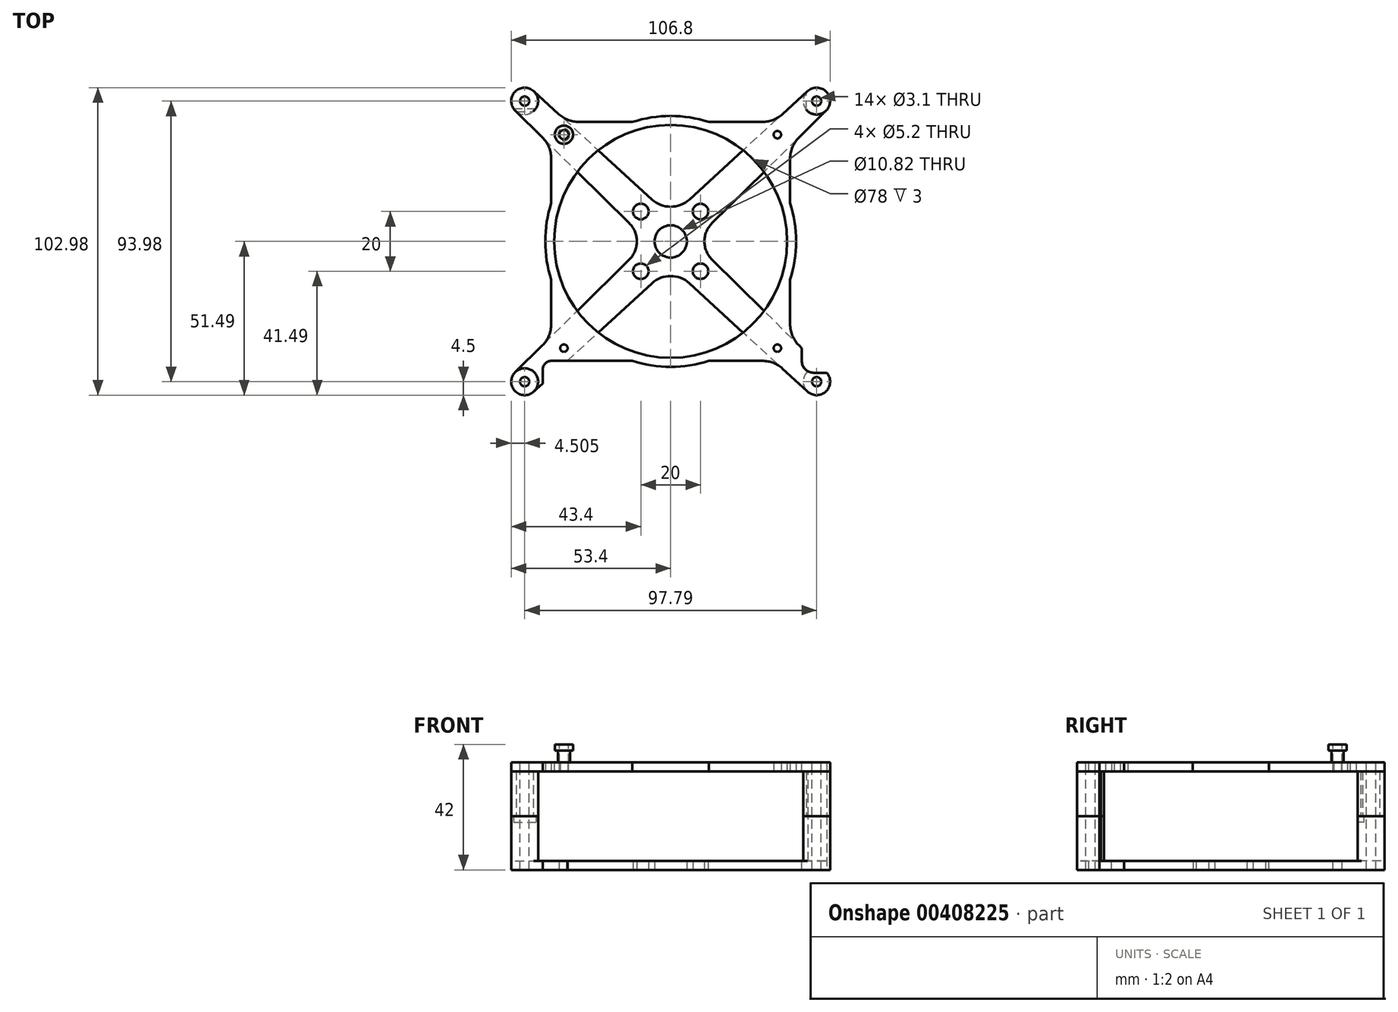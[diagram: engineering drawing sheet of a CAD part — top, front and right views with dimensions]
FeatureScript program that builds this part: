
annotation { "Feature Type Name" : "Feature", "Feature Type Description" : "" }
export const myFeature = defineFeature(function(context is Context, id is Id, definition is map)
    precondition{}
    {
        {
            var Q0;
            Q0=qCreatedBy(makeId("Top.planeOp"),FACE);
            var sketch = newSketch(context, id + "F0", { "sketchPlane" : qUnion([Q0])});
            skLineSegment(sketch, "E0.rect.bottom", {"start": v(48.9, 46.99) * mm, "end": v(-48.9, 46.99) * mm, "construction": true});
            skLineSegment(sketch, "E0.rect.top", {"start": v(48.9, -47) * mm, "end": v(-48.9, -47) * mm, "construction": true});
            skLineSegment(sketch, "E0.rect.left", {"start": v(48.9, 46.99) * mm, "end": v(48.9, -47) * mm, "construction": true});
            skLineSegment(sketch, "E0.rect.right", {"start": v(-48.9, 46.99) * mm, "end": v(-48.9, -47) * mm, "construction": true});
            skPoint(sketch, "E0.rect.middle", {"position": v(0, 0) * mm});
            skLineSegment(sketch, "E1.rect.bottom", {"start": v(10, 10) * mm, "end": v(-10, 10) * mm, "construction": true});
            skLineSegment(sketch, "E1.rect.top", {"start": v(10, -10) * mm, "end": v(-10, -10) * mm, "construction": true});
            skLineSegment(sketch, "E1.rect.left", {"start": v(10, 10) * mm, "end": v(10, -10) * mm, "construction": true});
            skLineSegment(sketch, "E1.rect.right", {"start": v(-10, 10) * mm, "end": v(-10, -10) * mm, "construction": true});
            skCircle(sketch, "E2", {"center": v(-10, 10) * mm, "radius": 2.6 * mm});
            skCircle(sketch, "E3", {"center": v(10, 10) * mm, "radius": 2.6 * mm});
            skCircle(sketch, "E4", {"center": v(10, -10) * mm, "radius": 2.6 * mm});
            skCircle(sketch, "E5", {"center": v(-10, -10) * mm, "radius": 2.6 * mm});
            skArc(sketch, "E6", {"start": v(-45.86, 50.3) * mm, "mid": v(-52.16, 50.1) * mm, "end": v(-52.06, 43.79) * mm});
            skArc(sketch, "E7", {"start": v(52.06, 43.79) * mm, "mid": v(52.16, 50.1) * mm, "end": v(45.86, 50.3) * mm});
            skArc(sketch, "E8", {"start": v(45.86, -50.3) * mm, "mid": v(52.16, -50.1) * mm, "end": v(52.06, -43.79) * mm});
            skArc(sketch, "E9", {"start": v(-52.06, -43.79) * mm, "mid": v(-52.16, -50.1) * mm, "end": v(-45.86, -50.3) * mm});
            skCircle(sketch, "E10", {"center": v(-10, -10) * mm, "radius": 5.5 * mm, "construction": true});
            skCircle(sketch, "E11", {"center": v(10, -10) * mm, "radius": 5.5 * mm, "construction": true});
            skCircle(sketch, "E12", {"center": v(-10, 10) * mm, "radius": 5.5 * mm, "construction": true});
            skCircle(sketch, "E13", {"center": v(10, 10) * mm, "radius": 5.5 * mm, "construction": true});
            skArc(sketch, "E14", {"start": v(-13.86, -6.09) * mm, "mid": v(-11.32, 0) * mm, "end": v(-13.86, 6.09) * mm});
            skLineSegment(sketch, "E15", {"start": v(-52.06, -43.79) * mm, "end": v(-13.86, -6.09) * mm});
            skLineSegment(sketch, "E16", {"start": v(-45.86, -50.3) * mm, "end": v(-6.28, -14.06) * mm});
            skLineSegment(sketch, "E17", {"start": v(45.86, 50.3) * mm, "end": v(6.28, 14.06) * mm});
            skLineSegment(sketch, "E18", {"start": v(52.06, 43.79) * mm, "end": v(13.86, 6.09) * mm});
            skLineSegment(sketch, "E19", {"start": v(-52.06, 43.79) * mm, "end": v(-13.86, 6.09) * mm});
            skLineSegment(sketch, "E20", {"start": v(-45.86, 50.3) * mm, "end": v(-6.28, 14.06) * mm});
            skLineSegment(sketch, "E21", {"start": v(45.86, -50.3) * mm, "end": v(6.28, -14.06) * mm});
            skLineSegment(sketch, "E22", {"start": v(52.06, -43.79) * mm, "end": v(13.86, -6.09) * mm});
            skArc(sketch, "E23", {"start": v(-6.28, 14.06) * mm, "mid": v(0, 11.61) * mm, "end": v(6.28, 14.06) * mm});
            skArc(sketch, "E24", {"start": v(13.86, 6.09) * mm, "mid": v(11.32, 0) * mm, "end": v(13.86, -6.09) * mm});
            skArc(sketch, "E25", {"start": v(6.28, -14.06) * mm, "mid": v(0, -11.61) * mm, "end": v(-6.28, -14.06) * mm});
            skCircle(sketch, "E26", {"center": v(0, 0) * mm, "radius": 5.4 * mm});
            skSolve(sketch);
        }
        {
            var Q0;
            Q0=qSketchRegion(id+"F0",true);
            extrude(context, id + "F1", {"entities" : qUnion([Q0]), "depth" : 3 * mm});
        }
        {
            var Q0;
            Q0=makeQuery(id+"F1.opExtrude","CAP_FACE",FACE,{"disambiguationData":[OSD([sQuery(id+"F0.wireOp",EDGE,"d0fabe0d-cebb-4a5e-acc7-4882b4730778"),sQuery(id+"F0.wireOp",EDGE,"8b31ac3e-8670-4111-bd45-4e3589581e22"),sQuery(id+"F0.wireOp",EDGE,"b8c4f240-0c61-4009-8258-f043c920e522"),sQuery(id+"F0.wireOp",EDGE,"c1348664-0ed1-4957-8f92-31a3f3ab937f"),sQuery(id+"F0.wireOp",EDGE,"E2"),sQuery(id+"F0.wireOp",EDGE,"E3"),sQuery(id+"F0.wireOp",EDGE,"E4"),sQuery(id+"F0.wireOp",EDGE,"E5"),sQuery(id+"F0.wireOp",EDGE,"E6"),sQuery(id+"F0.wireOp",EDGE,"E7"),sQuery(id+"F0.wireOp",EDGE,"E8"),sQuery(id+"F0.wireOp",EDGE,"E9"),sQuery(id+"F0.wireOp",EDGE,"E14"),sQuery(id+"F0.wireOp",EDGE,"E15"),sQuery(id+"F0.wireOp",EDGE,"E16"),sQuery(id+"F0.wireOp",EDGE,"E17"),sQuery(id+"F0.wireOp",EDGE,"E18"),sQuery(id+"F0.wireOp",EDGE,"E19"),sQuery(id+"F0.wireOp",EDGE,"E20"),sQuery(id+"F0.wireOp",EDGE,"E21"),sQuery(id+"F0.wireOp",EDGE,"E22"),sQuery(id+"F0.wireOp",EDGE,"E23"),sQuery(id+"F0.wireOp",EDGE,"E24"),sQuery(id+"F0.wireOp",EDGE,"E25"),sQuery(id+"F0.wireOp",EDGE,"E26")])],"isStart":false});
            var sketch = newSketch(context, id + "F2", { "sketchPlane" : qUnion([Q0])});
            skCircle(sketch, "E27", {"center": v(-48.9, 46.99) * mm, "radius": 4.5 * mm});
            skCircle(sketch, "E28", {"center": v(48.9, 46.99) * mm, "radius": 4.5 * mm});
            skCircle(sketch, "E29", {"center": v(48.9, -47) * mm, "radius": 4.5 * mm});
            skCircle(sketch, "E30", {"center": v(-48.9, -47) * mm, "radius": 4.5 * mm});
            skSolve(sketch);
        }
        {
            var Q0;
            Q0=qSketchRegion(id+"F2",true);
            extrude(context, id + "F3", {"entities" : qUnion([Q0]), "operationType" : NewBodyOperationType.ADD, "depth" : 15 * mm});
        }
        {
            var Q0;
            Q0=makeQuery(id+"F3.opExtrude","CAP_FACE",FACE,{"disambiguationData":[OSD([sQuery(id+"F2.wireOp",EDGE,"E27")])],"isStart":false});
            var sketch = newSketch(context, id + "F4", { "sketchPlane" : qUnion([Q0])});
            skCircle(sketch, "E31", {"center": v(-48.9, 46.99) * mm, "radius": 1.25 * mm});
            skCircle(sketch, "E32", {"center": v(48.9, 46.99) * mm, "radius": 1.25 * mm});
            skCircle(sketch, "E33", {"center": v(-48.9, -47) * mm, "radius": 1.25 * mm});
            skCircle(sketch, "E34", {"center": v(48.9, -47) * mm, "radius": 1.25 * mm});
            skSolve(sketch);
        }
        {
            var Q0;
            Q0=qSketchRegion(id+"F4",true);
            extrude(context, id + "F5", {"entities" : qUnion([Q0]), "operationType" : NewBodyOperationType.REMOVE, "endBound" : BoundingType.THROUGH_ALL, "oppositeDirection" : true, "depth" : 25 * mm});
        }
        {
            var Q0;
            Q0=makeQuery(id+"F3.opExtrude","CAP_FACE",FACE,{"disambiguationData":[OSD([sQuery(id+"F2.wireOp",EDGE,"E27")])],"isStart":false});
            var sketch = newSketch(context, id + "F6", { "sketchPlane" : qUnion([Q0])});
            skArc(sketch, "E35", {"start": v(-46.07, 43.49) * mm, "mid": v(-48.9, 51.49) * mm, "end": v(-51.72, 43.49) * mm});
            skArc(sketch, "E36", {"start": v(45.4, 44.16) * mm, "mid": v(53.4, 47) * mm, "end": v(45.4, 49.82) * mm});
            skArc(sketch, "E37", {"start": v(46.07, -43.5) * mm, "mid": v(48.9, -51.5) * mm, "end": v(51.72, -43.5) * mm});
            skCircle(sketch, "E38", {"center": v(-48.9, -47) * mm, "radius": 4.5 * mm});
            skLineSegment(sketch, "E39", {"start": v(-51.72, 43.49) * mm, "end": v(-46.07, 43.49) * mm});
            skLineSegment(sketch, "E40", {"start": v(45.4, 44.16) * mm, "end": v(45.4, 49.82) * mm});
            skLineSegment(sketch, "E41", {"start": v(46.07, -43.5) * mm, "end": v(51.72, -43.5) * mm});
            skSolve(sketch);
        }
        {
            var Q0;
            Q0=qSketchRegion(id+"F6",true);
            extrude(context, id + "F7", {"entities" : qUnion([Q0]), "depth" : 15 * mm});
        }
        {
            var Q0;
            Q0=makeQuery(id+"F7.opExtrude","CAP_FACE",FACE,{"disambiguationData":[OSD([sQuery(id+"F6.wireOp",EDGE,"E35")])],"isStart":false});
            var sketch = newSketch(context, id + "F8", { "sketchPlane" : qUnion([Q0])});
            skLineSegment(sketch, "E42.rect.bottom", {"start": v(35.75, 35.75) * mm, "end": v(-35.75, 35.75) * mm, "construction": true});
            skLineSegment(sketch, "E42.rect.top", {"start": v(35.75, -35.75) * mm, "end": v(-35.75, -35.75) * mm, "construction": true});
            skLineSegment(sketch, "E42.rect.left", {"start": v(35.75, 35.75) * mm, "end": v(35.75, -35.75) * mm, "construction": true});
            skLineSegment(sketch, "E42.rect.right", {"start": v(-35.75, 35.75) * mm, "end": v(-35.75, -35.75) * mm, "construction": true});
            skPoint(sketch, "E42.rect.middle", {"position": v(0, 0) * mm});
            skCircle(sketch, "E43", {"center": v(-35.75, 35.75) * mm, "radius": 1.25 * mm});
            skCircle(sketch, "E44", {"center": v(35.75, 35.75) * mm, "radius": 1.25 * mm});
            skCircle(sketch, "E45", {"center": v(35.75, -35.75) * mm, "radius": 1.25 * mm});
            skCircle(sketch, "E46", {"center": v(-35.75, -35.75) * mm, "radius": 1.25 * mm});
            skCircle(sketch, "E47", {"center": v(0, 0) * mm, "radius": 39 * mm});
            skArc(sketch, "E48", {"start": v(-52.06, -43.79) * mm, "mid": v(-52.16, -50.1) * mm, "end": v(-45.86, -50.3) * mm});
            skArc(sketch, "E49", {"start": v(45.86, -50.3) * mm, "mid": v(52.16, -50.1) * mm, "end": v(52.06, -43.79) * mm});
            skArc(sketch, "E50", {"start": v(52.06, 43.79) * mm, "mid": v(52.16, 50.1) * mm, "end": v(45.86, 50.3) * mm});
            skArc(sketch, "E51", {"start": v(-45.86, 50.3) * mm, "mid": v(-52.16, 50.1) * mm, "end": v(-52.06, 43.79) * mm});
            skLineSegment(sketch, "E52", {"start": v(-52.06, 43.79) * mm, "end": v(-42.97, 34.82) * mm});
            skLineSegment(sketch, "E53", {"start": v(-45.86, 50.3) * mm, "end": v(-37.47, 42.63) * mm});
            skLineSegment(sketch, "E54", {"start": v(45.86, 50.3) * mm, "end": v(37.47, 42.63) * mm});
            skLineSegment(sketch, "E55", {"start": v(52.06, 43.79) * mm, "end": v(42.97, 34.82) * mm});
            skLineSegment(sketch, "E56", {"start": v(52.06, -43.79) * mm, "end": v(42.97, -34.82) * mm});
            skLineSegment(sketch, "E57", {"start": v(45.86, -50.3) * mm, "end": v(37.47, -42.63) * mm});
            skLineSegment(sketch, "E58", {"start": v(-45.86, -50.3) * mm, "end": v(-37.47, -42.63) * mm});
            skLineSegment(sketch, "E59", {"start": v(-52.06, -43.79) * mm, "end": v(-42.97, -34.82) * mm});
            skLineSegment(sketch, "E60.rect.bottom", {"start": v(30.72, 40) * mm, "end": v(12.8, 40) * mm});
            skLineSegment(sketch, "E60.rect.top", {"start": v(30.72, -40) * mm, "end": v(12.8, -40) * mm});
            skLineSegment(sketch, "E60.rect.left", {"start": v(40, 27.7) * mm, "end": v(40, 12.8) * mm});
            skLineSegment(sketch, "E60.rect.right", {"start": v(-40, 27.7) * mm, "end": v(-40, 12.8) * mm});
            skPoint(sketch, "E61.orphan", {"position": v(-40, 40) * mm});
            skPoint(sketch, "E62.orphan", {"position": v(-40, -40) * mm});
            skLineSegment(sketch, "E63.trimOffspring", {"start": v(-40, -12.8) * mm, "end": v(-40, -27.7) * mm});
            skPoint(sketch, "E64.orphan", {"position": v(40, -40) * mm});
            skLineSegment(sketch, "E65.trimOffspring", {"start": v(40, -12.8) * mm, "end": v(40, -27.7) * mm});
            skPoint(sketch, "E66.orphan", {"position": v(40, 40) * mm});
            skArc(sketch, "E67.trimOffspring", {"start": v(12.8, 40) * mm, "mid": v(0, 42) * mm, "end": v(-12.8, 40) * mm});
            skLineSegment(sketch, "E68.trimOffspring", {"start": v(-12.8, 40) * mm, "end": v(-30.72, 40) * mm});
            skArc(sketch, "E69.trimOffspring", {"start": v(-40, 12.8) * mm, "mid": v(-42, 0) * mm, "end": v(-40, -12.8) * mm});
            skArc(sketch, "E70.trimOffspring", {"start": v(40, -12.8) * mm, "mid": v(42, 0) * mm, "end": v(40, 12.8) * mm});
            skLineSegment(sketch, "E71.trimOffspring", {"start": v(-12.8, -40) * mm, "end": v(-30.72, -40) * mm});
            skArc(sketch, "E72.trimOffspring", {"start": v(-12.8, -40) * mm, "mid": v(0, -42) * mm, "end": v(12.8, -40) * mm});
            skPoint(sketch, "E73.visualSharp", {"position": v(-40, 31.89) * mm});
            skArc(sketch, "E73.filletArc", {"start": v(-40, 27.7) * mm, "mid": v(-40.77, 31.56) * mm, "end": v(-42.97, 34.82) * mm});
            skPoint(sketch, "E74.visualSharp", {"position": v(-40, -31.89) * mm});
            skArc(sketch, "E74.filletArc", {"start": v(-42.97, -34.82) * mm, "mid": v(-40.77, -31.56) * mm, "end": v(-40, -27.7) * mm});
            skPoint(sketch, "E75.visualSharp", {"position": v(-34.6, -40) * mm});
            skArc(sketch, "E75.filletArc", {"start": v(-30.72, -40) * mm, "mid": v(-34.34, -40.68) * mm, "end": v(-37.47, -42.63) * mm});
            skPoint(sketch, "E76.visualSharp", {"position": v(34.6, -40) * mm});
            skArc(sketch, "E76.filletArc", {"start": v(37.47, -42.63) * mm, "mid": v(34.34, -40.68) * mm, "end": v(30.72, -40) * mm});
            skPoint(sketch, "E77.visualSharp", {"position": v(40, -31.89) * mm});
            skArc(sketch, "E77.filletArc", {"start": v(40, -27.7) * mm, "mid": v(40.77, -31.56) * mm, "end": v(42.97, -34.82) * mm});
            skPoint(sketch, "E78.visualSharp", {"position": v(40, 31.89) * mm});
            skArc(sketch, "E78.filletArc", {"start": v(42.97, 34.82) * mm, "mid": v(40.77, 31.56) * mm, "end": v(40, 27.7) * mm});
            skPoint(sketch, "E79.visualSharp", {"position": v(34.6, 40) * mm});
            skArc(sketch, "E79.filletArc", {"start": v(30.72, 40) * mm, "mid": v(34.34, 40.68) * mm, "end": v(37.47, 42.63) * mm});
            skPoint(sketch, "E80.visualSharp", {"position": v(-34.6, 40) * mm});
            skArc(sketch, "E80.filletArc", {"start": v(-37.47, 42.63) * mm, "mid": v(-34.34, 40.68) * mm, "end": v(-30.72, 40) * mm});
            skSolve(sketch);
        }
        {
            var Q0;
            Q0=qSketchRegion(id+"F8",true);
            extrude(context, id + "F9", {"entities" : qUnion([Q0]), "depth" : 3 * mm});
        }
        {
            var Q0;
            Q0=makeQuery(id+"F9.opExtrude","CAP_FACE",FACE,{"disambiguationData":[OSD([sQuery(id+"F8.wireOp",EDGE,"E43"),sQuery(id+"F8.wireOp",EDGE,"E44"),sQuery(id+"F8.wireOp",EDGE,"E45"),sQuery(id+"F8.wireOp",EDGE,"E46"),sQuery(id+"F8.wireOp",EDGE,"E47"),sQuery(id+"F8.wireOp",EDGE,"687bd6d6-6aec-43aa-978a-a651606573d6"),sQuery(id+"F8.wireOp",EDGE,"E48"),sQuery(id+"F8.wireOp",EDGE,"E49"),sQuery(id+"F8.wireOp",EDGE,"E50"),sQuery(id+"F8.wireOp",EDGE,"E51"),sQuery(id+"F8.wireOp",EDGE,"E52"),sQuery(id+"F8.wireOp",EDGE,"E53"),sQuery(id+"F8.wireOp",EDGE,"E54"),sQuery(id+"F8.wireOp",EDGE,"E55"),sQuery(id+"F8.wireOp",EDGE,"E56"),sQuery(id+"F8.wireOp",EDGE,"E57"),sQuery(id+"F8.wireOp",EDGE,"E58"),sQuery(id+"F8.wireOp",EDGE,"E59"),sQuery(id+"F8.wireOp",EDGE,"161f5221-b585-4942-8812-eb4c8e719fd1.trimOffspring"),sQuery(id+"F8.wireOp",EDGE,"33abffde-fc44-4a8e-acad-815204f06dd8.trimOffspring"),sQuery(id+"F8.wireOp",EDGE,"e672300c-3f6b-4d4b-81d5-837dd4541bc1.trimOffspring")])],"isStart":false});
            var sketch = newSketch(context, id + "F10", { "sketchPlane" : qUnion([Q0])});
            skCircle(sketch, "E81", {"center": v(-48.9, 46.99) * mm, "radius": 1.55 * mm});
            skCircle(sketch, "E82", {"center": v(48.9, 46.99) * mm, "radius": 1.55 * mm});
            skCircle(sketch, "E83", {"center": v(48.9, -47) * mm, "radius": 1.55 * mm});
            skCircle(sketch, "E84", {"center": v(-48.9, -47) * mm, "radius": 1.55 * mm});
            skSolve(sketch);
        }
        {
            var Q0;
            Q0=qSketchRegion(id+"F10",true);
            extrude(context, id + "F11", {"entities" : qUnion([Q0]), "operationType" : NewBodyOperationType.REMOVE, "endBound" : BoundingType.THROUGH_ALL, "oppositeDirection" : true, "depth" : 25 * mm});
        }
        {
            var Q0;
            Q0=makeQuery(id+"F9.opExtrude","CAP_FACE",FACE,{"disambiguationData":[OSD([sQuery(id+"F8.wireOp",EDGE,"E43"),sQuery(id+"F8.wireOp",EDGE,"E44"),sQuery(id+"F8.wireOp",EDGE,"E45"),sQuery(id+"F8.wireOp",EDGE,"E46"),sQuery(id+"F8.wireOp",EDGE,"E47"),sQuery(id+"F8.wireOp",EDGE,"687bd6d6-6aec-43aa-978a-a651606573d6"),sQuery(id+"F8.wireOp",EDGE,"E48"),sQuery(id+"F8.wireOp",EDGE,"E49"),sQuery(id+"F8.wireOp",EDGE,"E50"),sQuery(id+"F8.wireOp",EDGE,"E51"),sQuery(id+"F8.wireOp",EDGE,"E52"),sQuery(id+"F8.wireOp",EDGE,"E53"),sQuery(id+"F8.wireOp",EDGE,"E54"),sQuery(id+"F8.wireOp",EDGE,"E55"),sQuery(id+"F8.wireOp",EDGE,"E56"),sQuery(id+"F8.wireOp",EDGE,"E57"),sQuery(id+"F8.wireOp",EDGE,"E58"),sQuery(id+"F8.wireOp",EDGE,"E59"),sQuery(id+"F8.wireOp",EDGE,"161f5221-b585-4942-8812-eb4c8e719fd1.trimOffspring"),sQuery(id+"F8.wireOp",EDGE,"33abffde-fc44-4a8e-acad-815204f06dd8.trimOffspring"),sQuery(id+"F8.wireOp",EDGE,"e672300c-3f6b-4d4b-81d5-837dd4541bc1.trimOffspring")])],"isStart":false});
            var sketch = newSketch(context, id + "F12", { "sketchPlane" : qUnion([Q0])});
            skCircle(sketch, "E85", {"center": v(-35.75, 35.75) * mm, "radius": 2.05 * mm});
            skSolve(sketch);
        }
        {
            var Q0;
            Q0=qSketchRegion(id+"F12",true);
            extrude(context, id + "F13", {"entities" : qUnion([Q0]), "depth" : 4 * mm});
        }
        {
            var Q0;
            Q0=makeQuery(id+"F13.opExtrude","CAP_FACE",FACE,{"disambiguationData":[OSD([sQuery(id+"F12.wireOp",EDGE,"E85")])],"isStart":false});
            var sketch = newSketch(context, id + "F14", { "sketchPlane" : qUnion([Q0])});
            skCircle(sketch, "E86", {"center": v(-35.75, 35.75) * mm, "radius": 3.05 * mm});
            skSolve(sketch);
        }
        {
            var Q0;
            Q0=qSketchRegion(id+"F14",true);
            extrude(context, id + "F15", {"entities" : qUnion([Q0]), "operationType" : NewBodyOperationType.ADD, "depth" : 2 * mm});
        }
        {
            var Q0;
            Q0=makeQuery(id+"F15.opExtrude","CAP_FACE",FACE,{"disambiguationData":[OSD([sQuery(id+"F14.wireOp",EDGE,"E86")])],"isStart":false});
            var sketch = newSketch(context, id + "F16", { "sketchPlane" : qUnion([Q0])});
            skCircle(sketch, "E87", {"center": v(-35.75, 35.75) * mm, "radius": 1.55 * mm});
            skSolve(sketch);
        }
        {
            var Q0;
            Q0=qSketchRegion(id+"F16",true);
            extrude(context, id + "F17", {"entities" : qUnion([Q0]), "operationType" : NewBodyOperationType.REMOVE, "endBound" : BoundingType.THROUGH_ALL, "oppositeDirection" : true, "depth" : 25 * mm});
        }
        {
            var Q0;
            Q0=makeQuery(id+"F3.opExtrude","CAP_FACE",FACE,{"disambiguationData":[OSD([sQuery(id+"F2.wireOp",EDGE,"E27")])],"isStart":false});
            var sketch = newSketch(context, id + "F18", { "sketchPlane" : qUnion([Q0])});
            skLineSegment(sketch, "E88.bottom", {"start": v(-53.4, 44.49) * mm, "end": v(-44.4, 44.49) * mm});
            skLineSegment(sketch, "E88.top", {"start": v(-53.4, 41.49) * mm, "end": v(-44.4, 41.49) * mm});
            skLineSegment(sketch, "E88.left", {"start": v(-53.4, 44.49) * mm, "end": v(-53.4, 41.49) * mm});
            skLineSegment(sketch, "E88.right", {"start": v(-44.4, 44.49) * mm, "end": v(-44.4, 41.49) * mm});
            skPoint(sketch, "E89", {"position": v(-48.9, 46.99) * mm});
            skSolve(sketch);
        }
        {
            var Q0;
            Q0=qSketchRegion(id+"F18",true);
            extrude(context, id + "F19", {"entities" : qUnion([Q0]), "operationType" : NewBodyOperationType.REMOVE, "oppositeDirection" : true, "depth" : 2 * mm});
        }
        {
            var Q0;
            Q0=makeQuery(id+"F9.opExtrude","CAP_FACE",FACE,{"disambiguationData":[OSD([sQuery(id+"F8.wireOp",EDGE,"E43"),sQuery(id+"F8.wireOp",EDGE,"E44"),sQuery(id+"F8.wireOp",EDGE,"E45"),sQuery(id+"F8.wireOp",EDGE,"E46"),sQuery(id+"F8.wireOp",EDGE,"E47"),sQuery(id+"F8.wireOp",EDGE,"687bd6d6-6aec-43aa-978a-a651606573d6"),sQuery(id+"F8.wireOp",EDGE,"E48"),sQuery(id+"F8.wireOp",EDGE,"E49"),sQuery(id+"F8.wireOp",EDGE,"E50"),sQuery(id+"F8.wireOp",EDGE,"E51"),sQuery(id+"F8.wireOp",EDGE,"E52"),sQuery(id+"F8.wireOp",EDGE,"E53"),sQuery(id+"F8.wireOp",EDGE,"E54"),sQuery(id+"F8.wireOp",EDGE,"E55"),sQuery(id+"F8.wireOp",EDGE,"E56"),sQuery(id+"F8.wireOp",EDGE,"E57"),sQuery(id+"F8.wireOp",EDGE,"E58"),sQuery(id+"F8.wireOp",EDGE,"E59"),sQuery(id+"F8.wireOp",EDGE,"161f5221-b585-4942-8812-eb4c8e719fd1.trimOffspring"),sQuery(id+"F8.wireOp",EDGE,"33abffde-fc44-4a8e-acad-815204f06dd8.trimOffspring"),sQuery(id+"F8.wireOp",EDGE,"e672300c-3f6b-4d4b-81d5-837dd4541bc1.trimOffspring")])],"isStart":false});
            var sketch = newSketch(context, id + "F20", { "sketchPlane" : qUnion([Q0])});
            skLineSegment(sketch, "E90.bottom", {"start": v(47.9, -44) * mm, "end": v(52.9, -44) * mm});
            skLineSegment(sketch, "E90.top", {"start": v(43.9, -35) * mm, "end": v(52.9, -35) * mm});
            skLineSegment(sketch, "E90.left", {"start": v(43.9, -40) * mm, "end": v(43.9, -35) * mm});
            skLineSegment(sketch, "E90.right", {"start": v(52.9, -44) * mm, "end": v(52.9, -35) * mm});
            skPoint(sketch, "E91", {"position": v(48.9, -47) * mm});
            skPoint(sketch, "E92.visualSharp", {"position": v(43.9, -44) * mm});
            skArc(sketch, "E92.filletArc", {"start": v(43.9, -40) * mm, "mid": v(45.07, -42.82) * mm, "end": v(47.9, -44) * mm});
            skLineSegment(sketch, "E93.bottom", {"start": v(-42.9, -52.18) * mm, "end": v(-30.72, -52.18) * mm});
            skLineSegment(sketch, "E93.top", {"start": v(-39.9, -40) * mm, "end": v(-30.72, -40) * mm});
            skLineSegment(sketch, "E93.left", {"start": v(-42.9, -43) * mm, "end": v(-42.9, -52.18) * mm});
            skLineSegment(sketch, "E93.right", {"start": v(-30.72, -40) * mm, "end": v(-30.72, -52.18) * mm});
            skPoint(sketch, "E94", {"position": v(-48.9, -47) * mm});
            skPoint(sketch, "E95.visualSharp", {"position": v(-42.9, -40) * mm});
            skArc(sketch, "E95.filletArc", {"start": v(-39.9, -40) * mm, "mid": v(-42.02, -40.88) * mm, "end": v(-42.9, -43) * mm});
            skSolve(sketch);
        }
        {
            var Q0;
            Q0=qSketchRegion(id+"F20",true);
            extrude(context, id + "F21", {"entities" : qUnion([Q0]), "operationType" : NewBodyOperationType.REMOVE, "endBound" : BoundingType.THROUGH_ALL, "oppositeDirection" : true, "depth" : 25 * mm});
        }
    });
